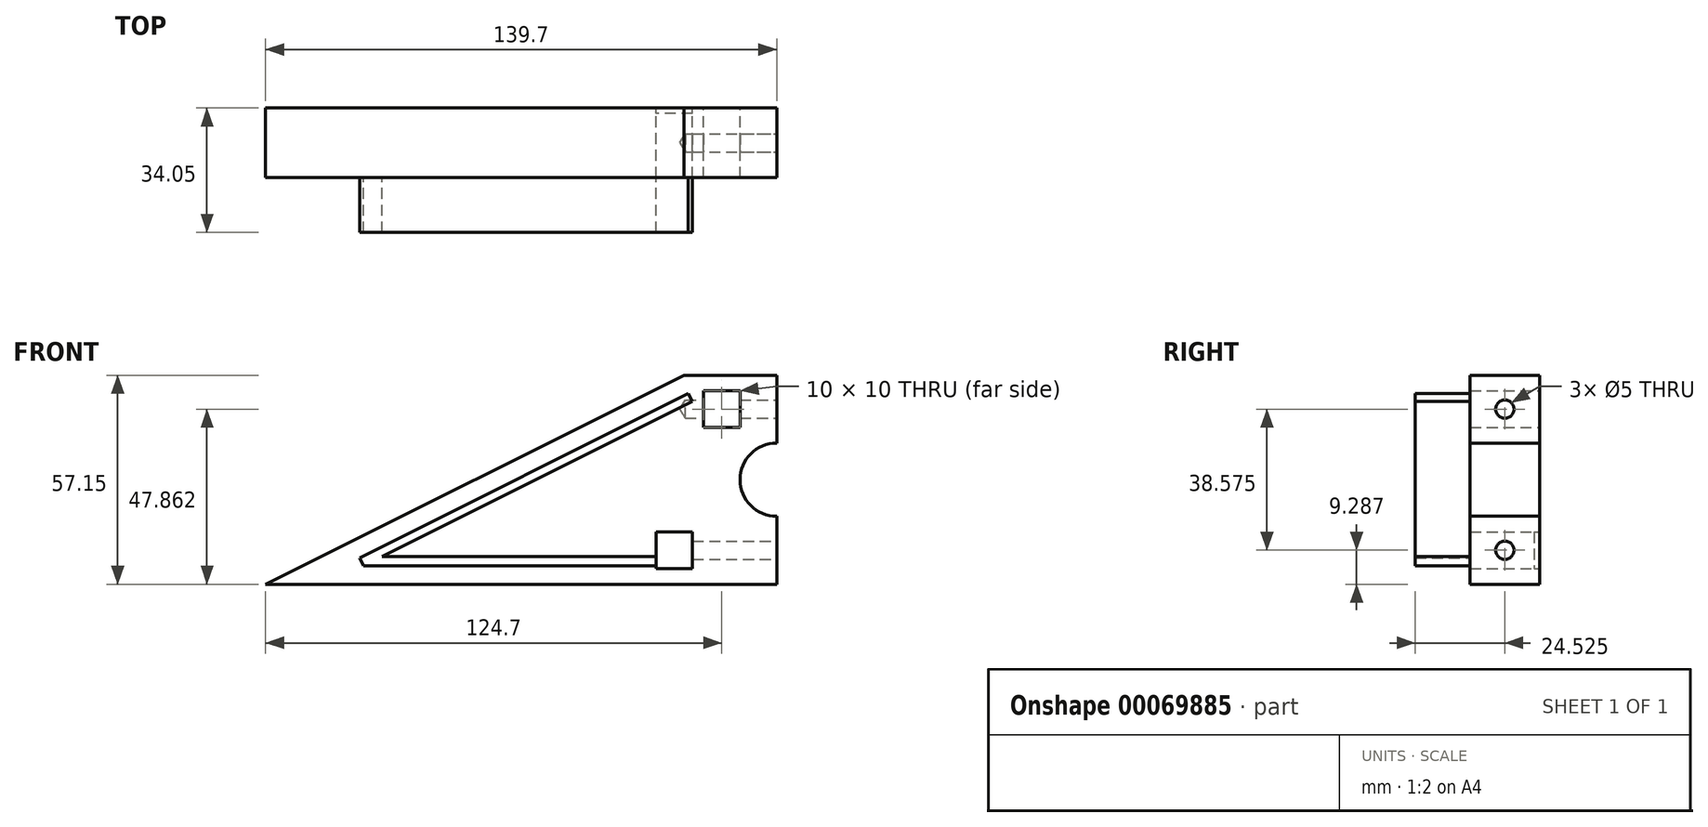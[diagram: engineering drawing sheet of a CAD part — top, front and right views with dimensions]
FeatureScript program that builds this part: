
annotation { "Feature Type Name" : "Feature", "Feature Type Description" : "" }
export const myFeature = defineFeature(function(context is Context, id is Id, definition is map)
    precondition{}
    {
        {
            var Q0;
            Q0=qCreatedBy(makeId("Front.planeOp"),FACE);
            var sketch = newSketch(context, id + "F0", { "sketchPlane" : qUnion([Q0])});
            skLineSegment(sketch, "E0", {"start": v(-69.85, 0) * mm, "end": v(69.85, 0) * mm});
            skLineSegment(sketch, "E1", {"start": v(69.85, 0) * mm, "end": v(69.85, 18.58) * mm});
            skLineSegment(sketch, "E2", {"start": v(69.85, 57.15) * mm, "end": v(44.45, 57.15) * mm});
            skLineSegment(sketch, "E3", {"start": v(-69.85, 0) * mm, "end": v(44.45, 57.15) * mm});
            skPoint(sketch, "E4", {"position": v(69.85, 28.57) * mm});
            skArc(sketch, "E5", {"start": v(69.85, 38.57) * mm, "mid": v(59.85, 28.57) * mm, "end": v(69.85, 18.58) * mm});
            skLineSegment(sketch, "E6.trimOffspring", {"start": v(69.85, 38.57) * mm, "end": v(69.85, 57.15) * mm});
            skPoint(sketch, "E7", {"position": v(69.85, 9.29) * mm});
            skLineSegment(sketch, "E8", {"start": v(69.85, 9.29) * mm, "end": v(41.85, 9.29) * mm, "construction": true});
            skLineSegment(sketch, "E9.bottom", {"start": v(46.85, 14.29) * mm, "end": v(36.85, 14.29) * mm});
            skLineSegment(sketch, "E9.top", {"start": v(46.85, 4.29) * mm, "end": v(36.85, 4.29) * mm});
            skLineSegment(sketch, "E9.left", {"start": v(46.85, 14.29) * mm, "end": v(46.85, 4.29) * mm});
            skLineSegment(sketch, "E9.right", {"start": v(36.85, 14.29) * mm, "end": v(36.85, 4.29) * mm});
            skPoint(sketch, "E10", {"position": v(41.85, 14.29) * mm});
            skPoint(sketch, "E11", {"position": v(36.85, 9.29) * mm});
            skPoint(sketch, "E12", {"position": v(41.85, 4.29) * mm});
            skPoint(sketch, "E13", {"position": v(46.85, 9.29) * mm});
            skLineSegment(sketch, "E14", {"start": v(41.85, 14.29) * mm, "end": v(41.85, 4.29) * mm, "construction": true});
            skLineSegment(sketch, "E15", {"start": v(46.85, 9.29) * mm, "end": v(36.85, 9.29) * mm, "construction": true});
            skPoint(sketch, "E16", {"position": v(41.85, 9.29) * mm});
            skPoint(sketch, "E17", {"position": v(69.85, 47.86) * mm});
            skLineSegment(sketch, "E18", {"start": v(69.85, 47.86) * mm, "end": v(54.85, 47.86) * mm, "construction": true});
            skLineSegment(sketch, "E19.bottom", {"start": v(59.85, 52.86) * mm, "end": v(49.85, 52.86) * mm});
            skLineSegment(sketch, "E19.top", {"start": v(59.85, 42.86) * mm, "end": v(49.85, 42.86) * mm});
            skLineSegment(sketch, "E19.left", {"start": v(59.85, 52.86) * mm, "end": v(59.85, 42.86) * mm});
            skLineSegment(sketch, "E19.right", {"start": v(49.85, 52.86) * mm, "end": v(49.85, 42.86) * mm});
            skPoint(sketch, "E20", {"position": v(54.85, 52.86) * mm});
            skPoint(sketch, "E21", {"position": v(54.85, 42.86) * mm});
            skPoint(sketch, "E22", {"position": v(59.85, 47.86) * mm});
            skPoint(sketch, "E23", {"position": v(49.85, 47.86) * mm});
            skLineSegment(sketch, "E24", {"start": v(54.85, 52.86) * mm, "end": v(54.85, 42.86) * mm, "construction": true});
            skLineSegment(sketch, "E25", {"start": v(59.85, 47.86) * mm, "end": v(49.85, 47.86) * mm, "construction": true});
            skPoint(sketch, "E26", {"position": v(54.85, 47.86) * mm});
            skSolve(sketch);
        }
        {
            var Q0;
            Q0=makeQuery(id+"F0.imprint","IMPRINT",FACE,{"disambiguationData":[TD([[makeQuery(id+"F0.imprint","IMPRINT",EDGE,{"derivedFrom":sQuery(id+"F0.wireOp",EDGE,"E0")}),1.0]])]});
            extrude(context, id + "F1", {"entities" : qUnion([Q0]), "depth" : 19.05 * mm});
        }
        {
            var Q0;
            Q0=makeQuery(id+"F1.opExtrude","CAP_FACE",FACE,{"disambiguationData":[OSD([sQuery(id+"F0.wireOp",EDGE,"E0"),sQuery(id+"F0.wireOp",EDGE,"E1"),sQuery(id+"F0.wireOp",EDGE,"E2"),sQuery(id+"F0.wireOp",EDGE,"E3"),sQuery(id+"F0.wireOp",EDGE,"E5"),sQuery(id+"F0.wireOp",EDGE,"E6.trimOffspring")])],"isStart":false});
            var sketch = newSketch(context, id + "F2", { "sketchPlane" : qUnion([Q0])});
            skLineSegment(sketch, "E27", {"start": v(12.07, 35.37) * mm, "end": v(-44.2, 7.24) * mm});
            skLineSegment(sketch, "E28", {"start": v(12.07, 35.37) * mm, "end": v(45.69, 52.18) * mm});
            skLineSegment(sketch, "E29", {"start": v(13.19, 33.13) * mm, "end": v(-38.08, 7.5) * mm});
            skLineSegment(sketch, "E30", {"start": v(13.19, 33.13) * mm, "end": v(46.8, 49.94) * mm});
            skLineSegment(sketch, "E31", {"start": v(-44.2, 7.24) * mm, "end": v(-43.08, 5) * mm});
            skPoint(sketch, "E32.orphan", {"position": v(-53.08, 0) * mm});
            skLineSegment(sketch, "E33", {"start": v(-43.08, 5) * mm, "end": v(50.86, 5) * mm});
            skLineSegment(sketch, "E34", {"start": v(36.78, 7.5) * mm, "end": v(-38.08, 7.5) * mm});
            skLineSegment(sketch, "E35", {"start": v(36.78, 7.5) * mm, "end": v(50.86, 7.5) * mm});
            skLineSegment(sketch, "E36", {"start": v(50.86, 7.5) * mm, "end": v(50.86, 5) * mm});
            skLineSegment(sketch, "E37", {"start": v(45.69, 52.18) * mm, "end": v(46.8, 49.94) * mm});
            skSolve(sketch);
        }
        {
            var Q0;
            Q0=makeQuery(id+"F2.imprint","IMPRINT",FACE,{"disambiguationData":[TD([[makeQuery(id+"F2.imprint","IMPRINT",EDGE,{"derivedFrom":sQuery(id+"F2.wireOp",EDGE,"E27")}),1.0]])]});
            extrude(context, id + "F3", {"entities" : qUnion([Q0]), "operationType" : NewBodyOperationType.ADD, "depth" : 15 * mm});
        }
        {
            var Q0;
            Q0=makeQuery(id+"F1.opExtrude","SWEPT_FACE",FACE,{"disambiguationData":[OSD([sQuery(id+"F0.wireOp",EDGE,"E1")])]});
            var sketch = newSketch(context, id + "F4", { "sketchPlane" : qUnion([Q0])});
            skPoint(sketch, "E38", {"position": v(-9.53, 18.58) * mm});
            skPoint(sketch, "E39", {"position": v(-19.05, 9.29) * mm});
            skPoint(sketch, "E40", {"position": v(-9.53, 0) * mm});
            skPoint(sketch, "E41", {"position": v(0, 9.29) * mm});
            skLineSegment(sketch, "E42", {"start": v(-9.53, 18.58) * mm, "end": v(-9.53, 0) * mm, "construction": true});
            skLineSegment(sketch, "E43", {"start": v(0, 9.29) * mm, "end": v(-19.05, 9.29) * mm, "construction": true});
            skPoint(sketch, "E44", {"position": v(-9.53, 9.29) * mm});
            skSolve(sketch);
        }
        {
            var Q0;
            Q0=sQuery(id+"F4.wireOp",VERTEX,"E44");
            var Q1;
            Q1=makeQuery(id+"F1.opExtrude","SWEPT_BODY",BODY,{"disambiguationData":[OSD([sQuery(id+"F0.wireOp",EDGE,"E0"),sQuery(id+"F0.wireOp",EDGE,"E1"),sQuery(id+"F0.wireOp",EDGE,"E2"),sQuery(id+"F0.wireOp",EDGE,"E3"),sQuery(id+"F0.wireOp",EDGE,"E5"),sQuery(id+"F0.wireOp",EDGE,"E6.trimOffspring")])]});
            hole(context, id + "F5", {"style" : HoleStyle.SIMPLE, "holeDiameter" : 5 * mm, "endStyle" : HoleEndStyle.BLIND, "holeDepth" : 30 * mm, "locations" : qUnion([Q0]), "scope" : qUnion([Q1])});
        }
        {
            var Q0;
            Q0=makeQuery(id+"F1.opExtrude","CAP_FACE",FACE,{"disambiguationData":[OSD([sQuery(id+"F0.wireOp",EDGE,"E0"),sQuery(id+"F0.wireOp",EDGE,"E1"),sQuery(id+"F0.wireOp",EDGE,"E2"),sQuery(id+"F0.wireOp",EDGE,"E3"),sQuery(id+"F0.wireOp",EDGE,"E5"),sQuery(id+"F0.wireOp",EDGE,"E6.trimOffspring"),sQuery(id+"F0.wireOp",EDGE,"E9.bottom"),sQuery(id+"F0.wireOp",EDGE,"E9.top"),sQuery(id+"F0.wireOp",EDGE,"E9.left"),sQuery(id+"F0.wireOp",EDGE,"E9.right")])],"isStart":true});
            var sketch = newSketch(context, id + "F6", { "sketchPlane" : qUnion([Q0])});
            skLineSegment(sketch, "E45", {"start": v(-36.85, 14.29) * mm, "end": v(-46.85, 14.29) * mm});
            skLineSegment(sketch, "E46", {"start": v(-46.85, 14.29) * mm, "end": v(-46.85, 4.29) * mm});
            skLineSegment(sketch, "E47", {"start": v(-46.85, 4.29) * mm, "end": v(-36.85, 4.29) * mm});
            skLineSegment(sketch, "E48", {"start": v(-36.85, 4.29) * mm, "end": v(-36.85, 14.29) * mm});
            skPoint(sketch, "E49", {"position": v(-69.85, 47.86) * mm});
            skLineSegment(sketch, "E50", {"start": v(-69.85, 47.86) * mm, "end": v(-59.85, 47.86) * mm, "construction": true});
            skPoint(sketch, "E51", {"position": v(-59.85, 47.86) * mm});
            skLineSegment(sketch, "E52.bottom", {"start": v(-64.85, 52.86) * mm, "end": v(-54.85, 52.86) * mm});
            skLineSegment(sketch, "E52.top", {"start": v(-64.85, 42.86) * mm, "end": v(-54.85, 42.86) * mm});
            skLineSegment(sketch, "E52.left", {"start": v(-64.85, 52.86) * mm, "end": v(-64.85, 42.86) * mm});
            skLineSegment(sketch, "E52.right", {"start": v(-54.85, 52.86) * mm, "end": v(-54.85, 42.86) * mm});
            skPoint(sketch, "E53", {"position": v(-59.85, 52.86) * mm});
            skPoint(sketch, "E54", {"position": v(-59.85, 42.86) * mm});
            skPoint(sketch, "E55", {"position": v(-64.85, 47.86) * mm});
            skPoint(sketch, "E56", {"position": v(-54.85, 47.86) * mm});
            skLineSegment(sketch, "E57", {"start": v(-59.85, 52.86) * mm, "end": v(-59.85, 42.86) * mm, "construction": true});
            skLineSegment(sketch, "E58", {"start": v(-64.85, 47.86) * mm, "end": v(-54.85, 47.86) * mm, "construction": true});
            skSolve(sketch);
        }
        {
            var Q0;
            Q0=makeQuery(id+"F6.imprint","IMPRINT",FACE,{"disambiguationData":[TD([[makeQuery(id+"F6.imprint","IMPRINT",EDGE,{"derivedFrom":sQuery(id+"F6.wireOp",EDGE,"E45")}),-1.0]])]});
            extrude(context, id + "F7", {"entities" : qUnion([Q0]), "oppositeDirection" : true, "depth" : 1.5 * mm});
        }
        {
            var Q0;
            Q0=makeQuery(id+"F1.opExtrude","SWEPT_FACE",FACE,{"disambiguationData":[OSD([sQuery(id+"F0.wireOp",EDGE,"E6.trimOffspring")])]});
            var sketch = newSketch(context, id + "F8", { "sketchPlane" : qUnion([Q0])});
            skPoint(sketch, "E59", {"position": v(-19.05, 47.86) * mm});
            skPoint(sketch, "E60", {"position": v(0, 47.86) * mm});
            skPoint(sketch, "E61", {"position": v(-9.53, 57.15) * mm});
            skPoint(sketch, "E62", {"position": v(-9.53, 38.57) * mm});
            skLineSegment(sketch, "E63", {"start": v(-19.05, 47.86) * mm, "end": v(0, 47.86) * mm, "construction": true});
            skLineSegment(sketch, "E64", {"start": v(-9.53, 57.15) * mm, "end": v(-9.53, 38.57) * mm, "construction": true});
            skPoint(sketch, "E65", {"position": v(-9.53, 47.86) * mm});
            skSolve(sketch);
        }
        {
            var Q0;
            Q0=sQuery(id+"F8.wireOp",VERTEX,"E65");
            var Q1;
            Q1=makeQuery(id+"F1.opExtrude","SWEPT_BODY",BODY,{"disambiguationData":[OSD([sQuery(id+"F0.wireOp",EDGE,"E0"),sQuery(id+"F0.wireOp",EDGE,"E1"),sQuery(id+"F0.wireOp",EDGE,"E2"),sQuery(id+"F0.wireOp",EDGE,"E3"),sQuery(id+"F0.wireOp",EDGE,"E5"),sQuery(id+"F0.wireOp",EDGE,"E6.trimOffspring"),sQuery(id+"F0.wireOp",EDGE,"E9.bottom"),sQuery(id+"F0.wireOp",EDGE,"E9.top"),sQuery(id+"F0.wireOp",EDGE,"E9.left"),sQuery(id+"F0.wireOp",EDGE,"E9.right"),sQuery(id+"F0.wireOp",EDGE,"E19.bottom"),sQuery(id+"F0.wireOp",EDGE,"E19.top"),sQuery(id+"F0.wireOp",EDGE,"E19.left"),sQuery(id+"F0.wireOp",EDGE,"E19.right")])]});
            hole(context, id + "F9", {"style" : HoleStyle.SIMPLE, "holeDiameter" : 5 * mm, "endStyle" : HoleEndStyle.BLIND, "holeDepth" : 25 * mm, "locations" : qUnion([Q0]), "scope" : qUnion([Q1])});
        }
    });
